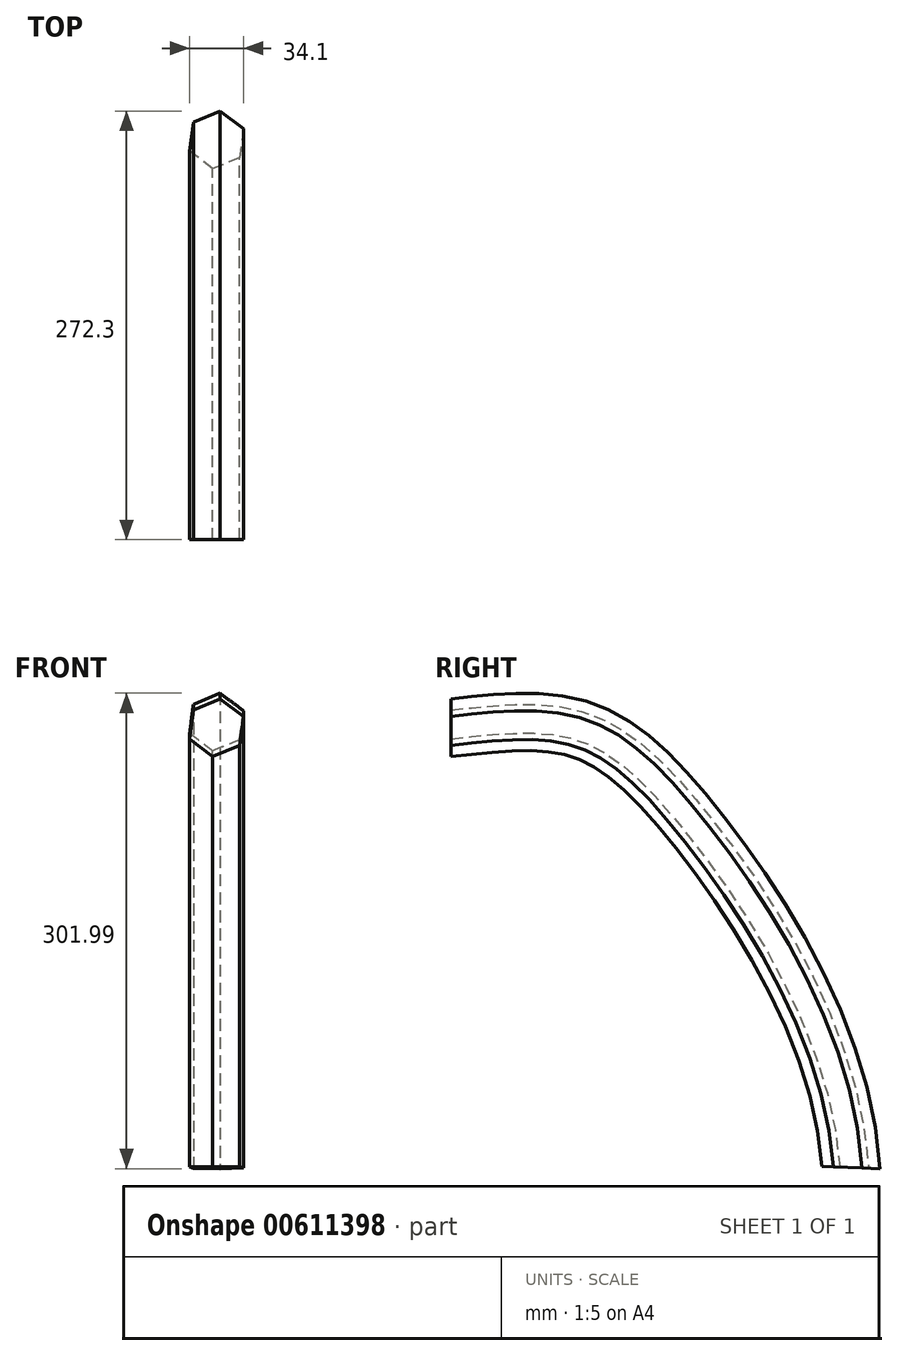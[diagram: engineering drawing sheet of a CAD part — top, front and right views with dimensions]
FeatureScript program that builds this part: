
annotation { "Feature Type Name" : "Feature", "Feature Type Description" : "" }
export const myFeature = defineFeature(function(context is Context, id is Id, definition is map)
    precondition{}
    {
        {
            var Q0;
            Q0=qCreatedBy(makeId("Front.planeOp"),FACE);
            var sketch = newSketch(context, id + "F0", { "sketchPlane" : qUnion([Q0])});
            skCircle(sketch, "E0.cCircle", {"center": v(0, 0) * mm, "radius": 18.47 * mm, "construction": true});
            skLineSegment(sketch, "E0.0", {"start": v(-14.68, 11.21) * mm, "end": v(2.37, 18.32) * mm});
            skLineSegment(sketch, "E0.1", {"start": v(2.37, 18.32) * mm, "end": v(17.05, 7.1) * mm});
            skLineSegment(sketch, "E0.2", {"start": v(17.05, 7.1) * mm, "end": v(14.68, -11.21) * mm});
            skLineSegment(sketch, "E0.3", {"start": v(14.68, -11.21) * mm, "end": v(-2.37, -18.32) * mm});
            skLineSegment(sketch, "E0.4", {"start": v(-2.37, -18.32) * mm, "end": v(-17.05, -7.1) * mm});
            skLineSegment(sketch, "E0.5", {"start": v(-17.05, -7.1) * mm, "end": v(-14.68, 11.21) * mm});
            skSolve(sketch);
        }
        {
            var Q0;
            Q0=qCreatedBy(makeId("Right.planeOp"),FACE);
            var sketch = newSketch(context, id + "F1", { "sketchPlane" : qUnion([Q0])});
            skFitSpline(sketch, "E1", {"points": [v(0, 0) * mm, v(78.28, 0) * mm, v(152.4, -59.49) * mm, v(254, -279.4) * mm], "startDerivative": vector(294.2, 31.13) * mm, "endDerivative": vector(36.32, -560.43) * mm});
            skSolve(sketch);
        }
        {
            var Q0;
            Q0=makeQuery(id+"F0.imprint","IMPRINT",FACE,{"disambiguationData":[TD([[makeQuery(id+"F0.imprint","IMPRINT",EDGE,{"derivedFrom":sQuery(id+"F0.wireOp",EDGE,"f168c249-aed6-49d2-8266-ad3b65776f04.0")}),-1.0]])]});
            var Q1;
            Q1=makeQuery(id+"F0.imprint","IMPRINT",FACE,{"disambiguationData":[TD([[makeQuery(id+"F0.imprint","IMPRINT",EDGE,{"derivedFrom":sQuery(id+"F0.wireOp",EDGE,"E0.0")}),-1.0]])]});
            var Q2;
            Q2=sQuery(id+"F1.wireOp",EDGE,"E1");
            sweep(context, id + "F2", {"profiles" : qUnion([Q0, Q1]), "path" : qUnion([Q2])});
        }
    });
